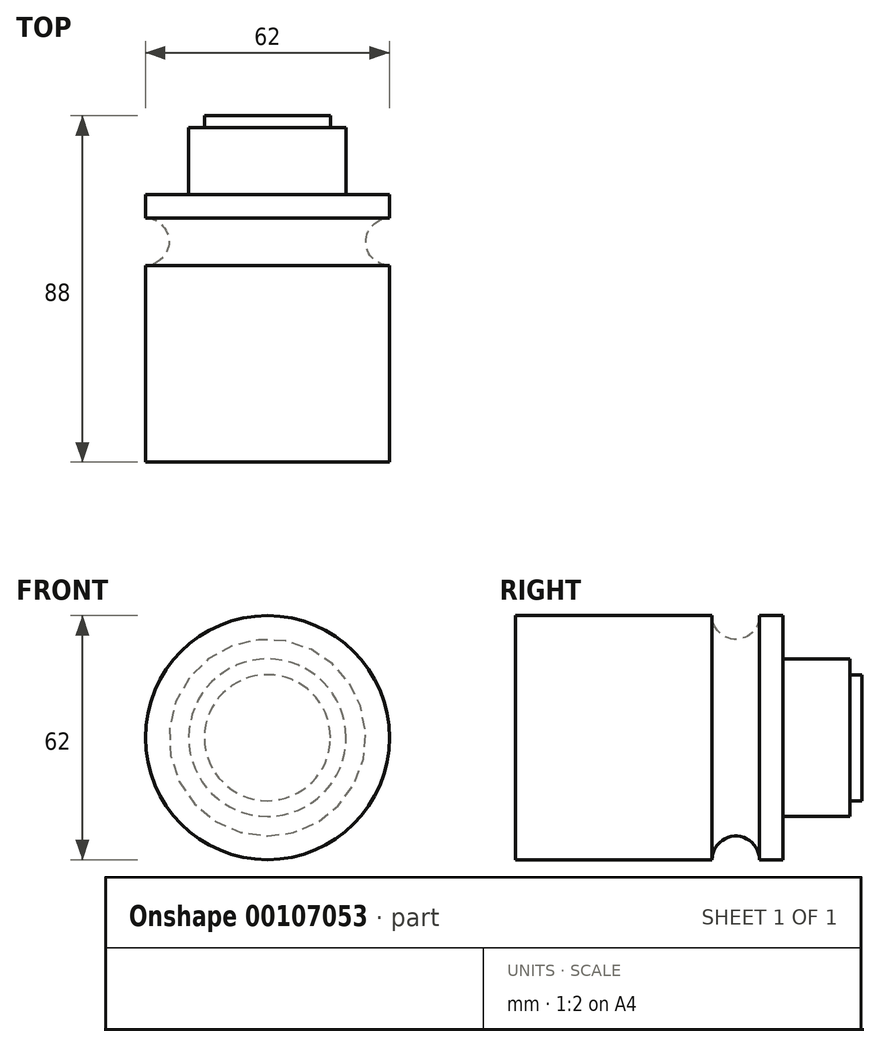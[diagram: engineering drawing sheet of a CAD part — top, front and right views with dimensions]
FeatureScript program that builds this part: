
annotation { "Feature Type Name" : "Feature", "Feature Type Description" : "" }
export const myFeature = defineFeature(function(context is Context, id is Id, definition is map)
    precondition{}
    {
        {
            var Q0;
            Q0=qCreatedBy(makeId("Right.planeOp"),FACE);
            var sketch = newSketch(context, id + "F0", { "sketchPlane" : qUnion([Q0])});
            skLineSegment(sketch, "E0", {"start": v(88, 0) * mm, "end": v(88, 16) * mm});
            skLineSegment(sketch, "E1", {"start": v(88, 16) * mm, "end": v(85, 16) * mm});
            skLineSegment(sketch, "E2", {"start": v(85, 16) * mm, "end": v(85, 20) * mm});
            skLineSegment(sketch, "E3", {"start": v(85, 20) * mm, "end": v(68, 20) * mm});
            skLineSegment(sketch, "E4", {"start": v(68, 20) * mm, "end": v(68, 31) * mm});
            skLineSegment(sketch, "E5", {"start": v(0, 31) * mm, "end": v(0, 0) * mm});
            skLineSegment(sketch, "E6", {"start": v(0, 31) * mm, "end": v(50, 31) * mm});
            skLineSegment(sketch, "E7", {"start": v(62, 31) * mm, "end": v(68, 31) * mm});
            skArc(sketch, "E8", {"start": v(50, 31) * mm, "mid": v(56, 25) * mm, "end": v(62, 31) * mm});
            skLineSegment(sketch, "E9", {"start": v(0, 0) * mm, "end": v(88, 0) * mm, "construction": true});
            skLineSegment(sketch, "E10", {"start": v(88, 0) * mm, "end": v(0, 0) * mm});
            skSolve(sketch);
        }
        {
            var Q0;
            Q0=qCreatedBy(makeId("Right.planeOp"),FACE);
            var sketch = newSketch(context, id + "F1", { "sketchPlane" : qUnion([Q0])});
            skLineSegment(sketch, "E11", {"start": v(0, 0) * mm, "end": v(0, 25) * mm});
            skLineSegment(sketch, "E12", {"start": v(0, 25) * mm, "end": v(1.5, 25) * mm});
            skLineSegment(sketch, "E13", {"start": v(1.5, 25) * mm, "end": v(1.5, 12.5) * mm});
            skLineSegment(sketch, "E14", {"start": v(1.5, 12.5) * mm, "end": v(12, 12.5) * mm});
            skLineSegment(sketch, "E15", {"start": v(12, 12.5) * mm, "end": v(12, 12.48) * mm});
            skLineSegment(sketch, "E16", {"start": v(12, 12.48) * mm, "end": v(15, 12.48) * mm});
            skLineSegment(sketch, "E17", {"start": v(15, 12.48) * mm, "end": v(15, 20.48) * mm});
            skLineSegment(sketch, "E18", {"start": v(15, 20.48) * mm, "end": v(20.5, 20.48) * mm});
            skLineSegment(sketch, "E19", {"start": v(20.5, 20.48) * mm, "end": v(20.5, 15.98) * mm});
            skLineSegment(sketch, "E20", {"start": v(20.5, 15.98) * mm, "end": v(28.5, 15.98) * mm});
            skLineSegment(sketch, "E21", {"start": v(28.5, 15.98) * mm, "end": v(28.5, 6) * mm});
            skLineSegment(sketch, "E22", {"start": v(28.5, 6) * mm, "end": v(88, 6) * mm});
            skLineSegment(sketch, "E23", {"start": v(0, 0) * mm, "end": v(88, 0) * mm, "construction": true});
            skSolve(sketch);
        }
        {
            var Q0;
            Q0 = qSketchRegion(id + "F0", true);
            var Q1;
            Q1=sQuery(id+"F1.wireOp",EDGE,"E23");
            revolve(context, id + "F2", {"entities" : qUnion([Q0]), "axis" : qUnion([Q1]), "revolveType" : RevolveType.FULL});
        }
    });
